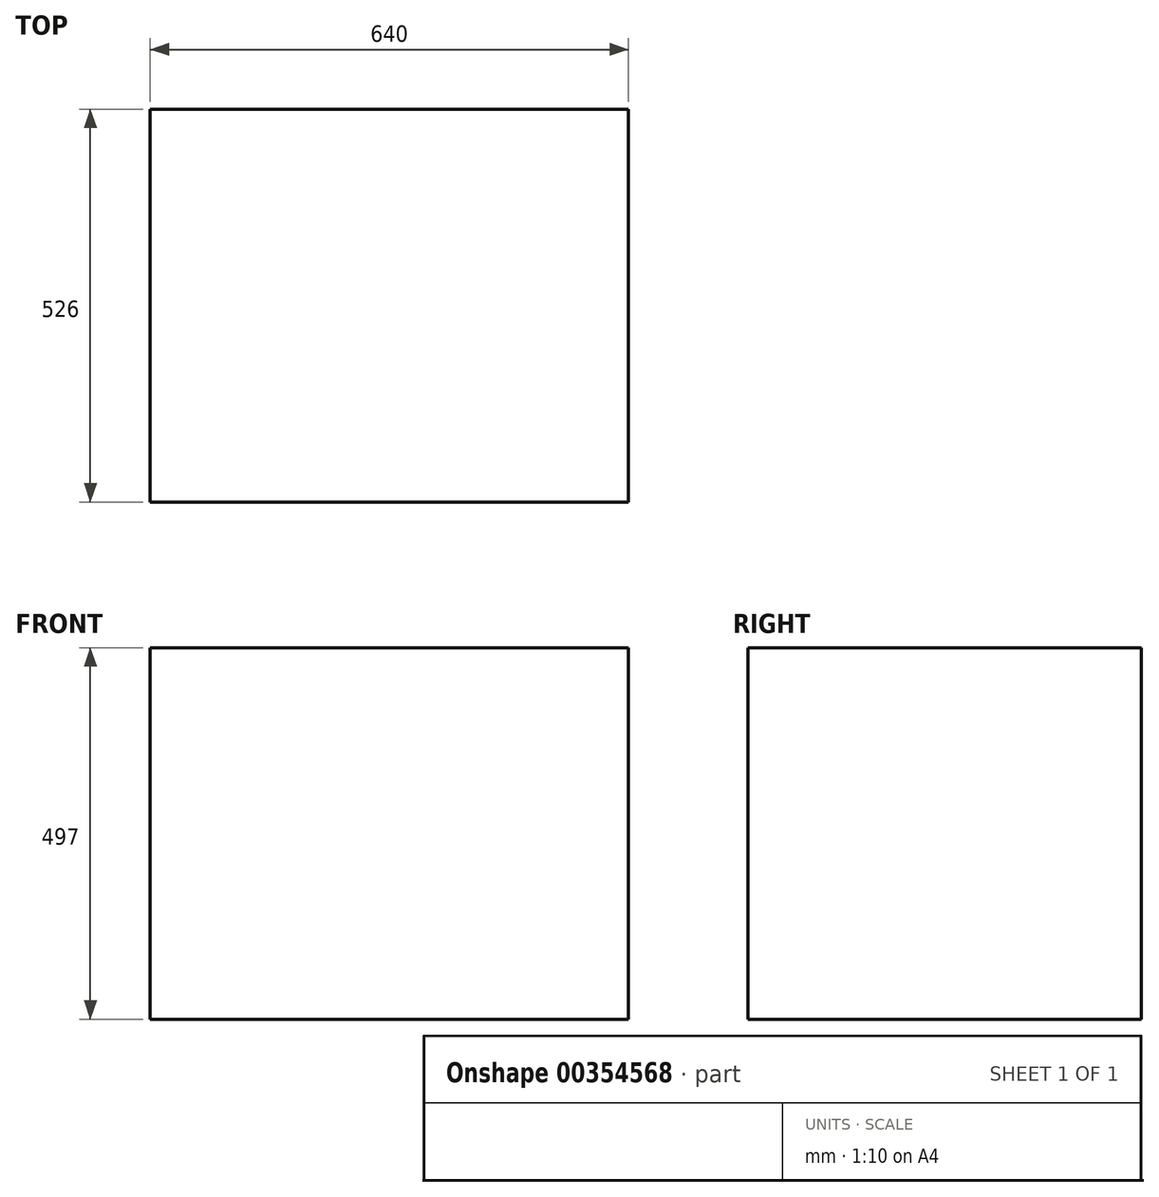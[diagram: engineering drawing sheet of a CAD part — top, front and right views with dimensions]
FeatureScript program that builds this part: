
annotation { "Feature Type Name" : "Feature", "Feature Type Description" : "" }
export const myFeature = defineFeature(function(context is Context, id is Id, definition is map)
    precondition{}
    {
        {
            var Q0;
            Q0=qCreatedBy(makeId("Top.planeOp"),FACE);
            var sketch = newSketch(context, id + "F0", { "sketchPlane" : qUnion([Q0])});
            skLineSegment(sketch, "E0.bottom", {"start": v(320, 263) * mm, "end": v(-320, 263) * mm});
            skLineSegment(sketch, "E0.top", {"start": v(320, -263) * mm, "end": v(-320, -263) * mm});
            skLineSegment(sketch, "E0.left", {"start": v(320, 263) * mm, "end": v(320, -263) * mm});
            skLineSegment(sketch, "E0.right", {"start": v(-320, 263) * mm, "end": v(-320, -263) * mm});
            skPoint(sketch, "E0.middle", {"position": v(0, 0) * mm});
            skSolve(sketch);
        }
        {
            var Q0;
            Q0=makeQuery(id+"F0.imprint","IMPRINT",FACE,{"disambiguationData":[TD([[makeQuery(id+"F0.imprint","IMPRINT",EDGE,{"derivedFrom":sQuery(id+"F0.wireOp",EDGE,"E0.bottom")}),1.0]])]});
            extrude(context, id + "F1", {"entities" : qUnion([Q0]), "depth" : 497 * mm});
        }
    });
